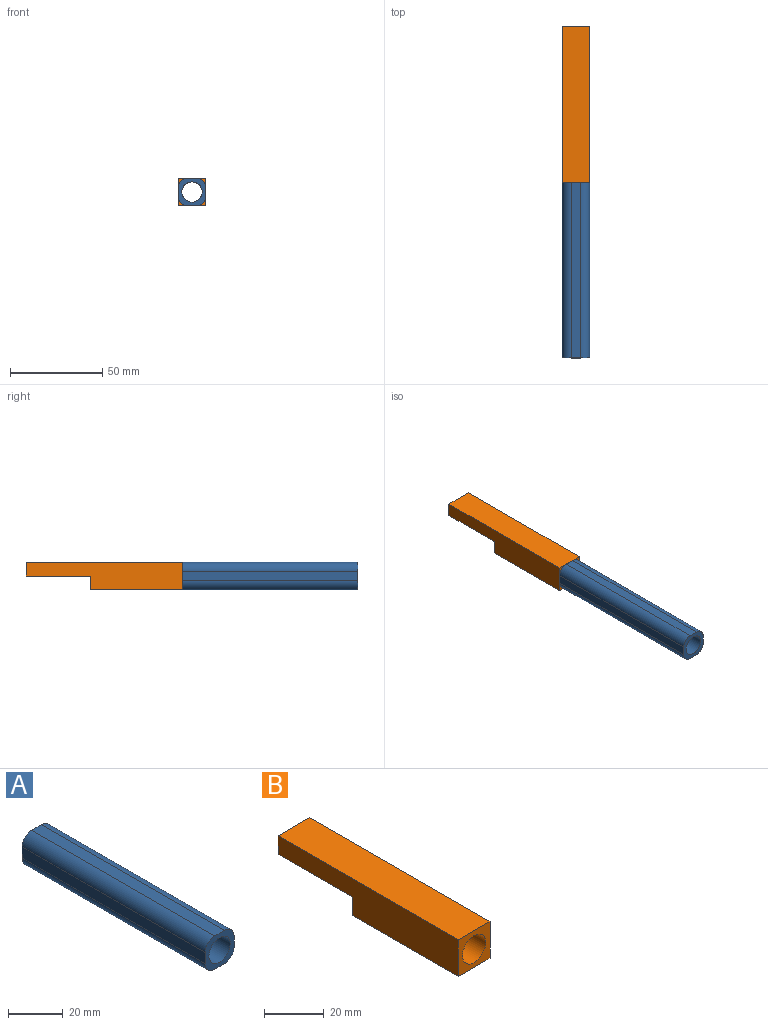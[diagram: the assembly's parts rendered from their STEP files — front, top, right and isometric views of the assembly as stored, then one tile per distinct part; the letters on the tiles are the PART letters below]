
ASSEMBLY  parts=2 mates=1
PART A: 11 faces, bbox 15x95x15 mm
  f0: plane 95x5mm, normal (0,0,1), area 475mm2, adj f4,f5,f7,f10
  f1: plane 95x5mm, normal (-1,0,0), area 475mm2, adj f4,f5,f7,f8
  f2: plane 95x5mm, normal (0,0,-1), area 475mm2, adj f4,f5,f8,f9
  f3: plane 95x5mm, normal (1,0,0), area 475mm2, adj f4,f5,f9,f10
  f4: plane 15x15mm, normal (0,-1,0), area 108.5mm2, adj f0,f1,f2,f3,f6,f7,f8,f9
  f5: plane 15x15mm, normal (0,1,0), area 108.5mm2, adj f0,f1,f2,f3,f6,f7,f8,f9
  f6: cylinder r=5.5mm len=95mm, axis (0,-1,0), area 3283mm2, adj f4,f5
  f7: cylinder r=5mm len=95mm, axis (0,-1,0), area 746.1mm2, adj f0,f1,f4,f5
  f8: cylinder r=5mm len=95mm, axis (0,1,0), area 746.1mm2, adj f1,f2,f4,f5
  f9: cylinder r=5mm len=95mm, axis (0,-1,0), area 746.1mm2, adj f2,f3,f4,f5
  f10: cylinder r=5mm len=95mm, axis (0,1,0), area 746.1mm2, adj f0,f3,f4,f5
PART B: 10 faces, bbox 15x85x15 mm
  f0: plane 85x15mm, normal (1,0,0), area 1012.5mm2, adj f1,f2,f4,f5,f8,f9
  f1: plane 15x7.5mm, normal (0,1,0), area 65mm2, adj f0,f2,f3,f6,f7,f8
  f2: plane 85x15mm, normal (0,0,1), area 1275mm2, adj f0,f1,f3,f5
  f3: plane 85x15mm, normal (-1,0,0), area 1012.5mm2, adj f1,f2,f4,f5,f7,f9
  f4: plane 50x15mm, normal (0,0,-1), area 750mm2, adj f0,f3,f5,f9
  f5: plane 15x15mm, normal (0,-1,0), area 130mm2, adj f0,f2,f3,f4,f6
  f6: cylinder r=5.5mm len=85mm, axis (0,-1,0), area 2332.6mm2, adj f1,f5,f7,f8,f9
  f7: plane 35x2mm, normal (0,0,-1), area 70mm2, adj f1,f3,f6,f9
  f8: plane 35x2mm, normal (0,0,-1), area 70mm2, adj f0,f1,f6,f9
  f9: plane 15x7.5mm, normal (0,1,0), area 65mm2, adj f0,f3,f4,f6,f7,f8
PLACE A t=(-15.69,-72.8,-22.28)mm
PLACE B t=(-15.69,12.2,-22.28)mm
MATE fastened A.f6 <-> B.f6  axis (0,-1,0) through (-15.29,-72.8,-20.96)mm
